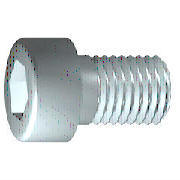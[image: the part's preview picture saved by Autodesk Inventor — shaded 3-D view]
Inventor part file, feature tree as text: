
AUTODESK INVENTOR PART (.ipt)
format: ipt  version: 2021.2 (Build 252289000, 289)  size: 194,560 bytes
history: native  units: mm (DEFAULTED — no unit token found)
features: sketch x2, other x1, extrude x1, plane x1, fillet x1
ambient origin geometry x7: Origin, YZ Plane, XY Plane, X Axis, Y Axis, Z Axis, Center Point
bodies: Solid1 (feature_tree)
feature tree (6):
  other  "Базовый элемент"
  extrude  "Паз"  Depth=7.5mm
  plane  "Work Plane1"
  fillet  "Fillet2"  Radius=0.306825mm
  sketch  "Эскиз1"
  sketch  "Эскиз2"
